# Revit family: QF_LANCER_TWINPOUR 44
name_source: partatom
category: Specialty Equipment
revit_build: Autodesk Revit 2015 (Build: 20140606_1530(x64)
units: mm (PartAtom-declared; Revit-internal decimal feet)

## types (1)
- QF_LANCER_TWINPOUR 44
    Apparent Power = 690 VA
    Cold Water Connection Height = 0 "
    Cold Water Flow = 0 GPM
    Cold Water Maximum Pressure = 0.00 psi
    Cold Water Minimum Pressure = 0.00 psi
    Cold Water RI Height = 0 "
    Cold Water Size = 0"
    Cold Water Temperature Recommended = 0 °F
    Conn Conduit = Yes
    Cycle = 60 Hz
    Depth = 31.13 "
    Description = ICE BEVERAGE DISPENSER
    Elec Conn Connection Height = 0 "
    Elec Conn RI Height = 0 "
    FL Amps = 6 A
    Foodservice Equipment Identifier = Yes
    Height = 39.38 "
    Identify Quantity as Lot = Yes
    Indirect Waste Connection Height = 0 "
    Indirect Waste Size = 2"
    Length = 44 "
    Manufacturer = LANCER
    Material and Finishes = QF_Plastic - Black - Matte
    Max Overcurrent Protection = 0 A
    Min Ckt Ampacity = 0 A
    Model = TWINPOUR 44
    Number of Poles = 1
    Phase = 1
    Volts = 115 V
    Waste Water Discharge Temperature = 0 °F
    Watts = 690 W
    Weight in Pounds = 745
